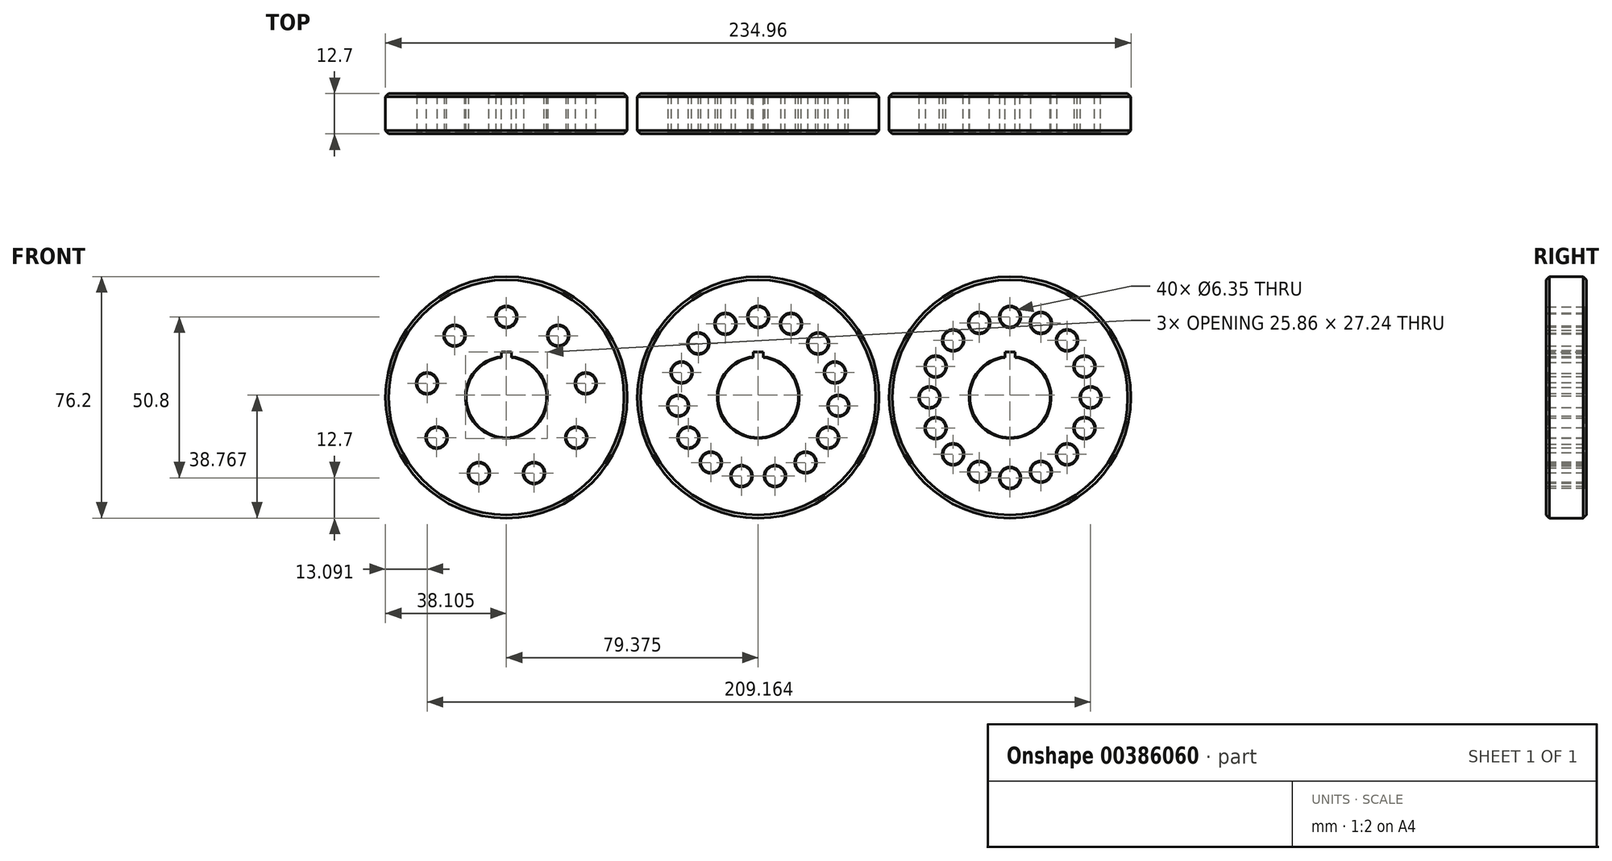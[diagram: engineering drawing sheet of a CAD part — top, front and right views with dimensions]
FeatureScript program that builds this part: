
annotation { "Feature Type Name" : "Feature", "Feature Type Description" : "" }
export const myFeature = defineFeature(function(context is Context, id is Id, definition is map)
    precondition{}
    {
        {
            var Q0;
            Q0=qCreatedBy(makeId("Front.planeOp"),FACE);
            var sketch = newSketch(context, id + "F0", { "sketchPlane" : qUnion([Q0])});
            skCircle(sketch, "E0", {"center": v(0, 0) * mm, "radius": 38.1 * mm});
            skCircle(sketch, "E1", {"center": v(-79.38, 0) * mm, "radius": 38.1 * mm});
            skCircle(sketch, "E2", {"center": v(79.38, 0) * mm, "radius": 38.1 * mm});
            skCircle(sketch, "E3", {"center": v(0, 25.4) * mm, "radius": 3.18 * mm});
            skCircle(sketch, "E4.1.0", {"center": v(-10.33, 23.2) * mm, "radius": 3.18 * mm});
            skCircle(sketch, "E4.2.0", {"center": v(-18.88, 17) * mm, "radius": 3.17 * mm});
            skCircle(sketch, "E4.3.0", {"center": v(-24.16, 7.85) * mm, "radius": 3.18 * mm});
            skCircle(sketch, "E4.4.0", {"center": v(-25.26, -2.66) * mm, "radius": 3.18 * mm});
            skCircle(sketch, "E4.5.0", {"center": v(-22, -12.7) * mm, "radius": 3.18 * mm});
            skCircle(sketch, "E4.6.0", {"center": v(-14.93, -20.55) * mm, "radius": 3.18 * mm});
            skCircle(sketch, "E4.7.0", {"center": v(-5.28, -24.84) * mm, "radius": 3.18 * mm});
            skCircle(sketch, "E4.8.0", {"center": v(5.28, -24.84) * mm, "radius": 3.18 * mm});
            skCircle(sketch, "E4.9.0", {"center": v(14.93, -20.55) * mm, "radius": 3.18 * mm});
            skCircle(sketch, "E4.10.0", {"center": v(22, -12.7) * mm, "radius": 3.18 * mm});
            skCircle(sketch, "E4.11.0", {"center": v(25.26, -2.66) * mm, "radius": 3.18 * mm});
            skCircle(sketch, "E4.12.0", {"center": v(24.16, 7.85) * mm, "radius": 3.18 * mm});
            skCircle(sketch, "E4.13.0", {"center": v(18.88, 17) * mm, "radius": 3.18 * mm});
            skCircle(sketch, "E4.14.0", {"center": v(10.33, 23.2) * mm, "radius": 3.18 * mm});
            skCircle(sketch, "E5", {"center": v(-79.38, 25.4) * mm, "radius": 3.18 * mm});
            skCircle(sketch, "E6.1.0", {"center": v(-95.7, 19.46) * mm, "radius": 3.18 * mm});
            skCircle(sketch, "E6.2.0", {"center": v(-104.39, 4.41) * mm, "radius": 3.18 * mm});
            skCircle(sketch, "E6.3.0", {"center": v(-101.37, -12.7) * mm, "radius": 3.18 * mm});
            skCircle(sketch, "E6.4.0", {"center": v(-88.06, -23.87) * mm, "radius": 3.18 * mm});
            skCircle(sketch, "E6.5.0", {"center": v(-70.69, -23.87) * mm, "radius": 3.18 * mm});
            skCircle(sketch, "E6.6.0", {"center": v(-57.38, -12.7) * mm, "radius": 3.18 * mm});
            skCircle(sketch, "E6.7.0", {"center": v(-54.36, 4.41) * mm, "radius": 3.18 * mm});
            skCircle(sketch, "E6.8.0", {"center": v(-63.05, 19.46) * mm, "radius": 3.18 * mm});
            skCircle(sketch, "E7", {"center": v(79.38, 25.4) * mm, "radius": 3.18 * mm});
            skCircle(sketch, "E8.1.0", {"center": v(69.65, 23.47) * mm, "radius": 3.18 * mm});
            skCircle(sketch, "E8.2.0", {"center": v(61.41, 17.96) * mm, "radius": 3.18 * mm});
            skCircle(sketch, "E8.3.0", {"center": v(55.9, 9.72) * mm, "radius": 3.18 * mm});
            skCircle(sketch, "E8.4.0", {"center": v(53.98, 0) * mm, "radius": 3.18 * mm});
            skCircle(sketch, "E8.5.0", {"center": v(55.9, -9.72) * mm, "radius": 3.18 * mm});
            skCircle(sketch, "E8.6.0", {"center": v(61.41, -17.96) * mm, "radius": 3.18 * mm});
            skCircle(sketch, "E8.7.0", {"center": v(69.65, -23.47) * mm, "radius": 3.18 * mm});
            skCircle(sketch, "E8.8.0", {"center": v(79.38, -25.4) * mm, "radius": 3.18 * mm});
            skCircle(sketch, "E8.9.0", {"center": v(89.1, -23.47) * mm, "radius": 3.18 * mm});
            skCircle(sketch, "E8.10.0", {"center": v(97.34, -17.96) * mm, "radius": 3.18 * mm});
            skCircle(sketch, "E8.11.0", {"center": v(102.84, -9.72) * mm, "radius": 3.18 * mm});
            skCircle(sketch, "E8.12.0", {"center": v(104.78, 0) * mm, "radius": 3.18 * mm});
            skCircle(sketch, "E8.13.0", {"center": v(102.84, 9.72) * mm, "radius": 3.18 * mm});
            skCircle(sketch, "E8.14.0", {"center": v(97.34, 17.96) * mm, "radius": 3.18 * mm});
            skCircle(sketch, "E8.15.0", {"center": v(89.1, 23.47) * mm, "radius": 3.18 * mm});
            skCircle(sketch, "E9", {"center": v(-79.38, 0) * mm, "radius": 12.7 * mm});
            skCircle(sketch, "E10", {"center": v(0, 0) * mm, "radius": 12.7 * mm});
            skCircle(sketch, "E11", {"center": v(79.38, 0) * mm, "radius": 12.7 * mm});
            skLineSegment(sketch, "E12.bottom", {"start": v(-77.79, 14.29) * mm, "end": v(-80.96, 14.29) * mm});
            skLineSegment(sketch, "E12.top", {"start": v(-77.79, 11.11) * mm, "end": v(-80.96, 11.11) * mm});
            skLineSegment(sketch, "E12.left", {"start": v(-77.79, 14.29) * mm, "end": v(-77.79, 11.11) * mm});
            skLineSegment(sketch, "E12.right", {"start": v(-80.96, 14.29) * mm, "end": v(-80.96, 11.11) * mm});
            skPoint(sketch, "E12.middle", {"position": v(-79.38, 12.7) * mm});
            skLineSegment(sketch, "E13.bottom", {"start": v(1.59, 14.29) * mm, "end": v(-1.59, 14.29) * mm});
            skLineSegment(sketch, "E13.top", {"start": v(1.59, 11.11) * mm, "end": v(-1.59, 11.11) * mm});
            skLineSegment(sketch, "E13.left", {"start": v(1.59, 14.29) * mm, "end": v(1.59, 11.11) * mm});
            skLineSegment(sketch, "E13.right", {"start": v(-1.59, 14.29) * mm, "end": v(-1.59, 11.11) * mm});
            skPoint(sketch, "E13.middle", {"position": v(0, 12.7) * mm});
            skLineSegment(sketch, "E14.bottom", {"start": v(80.96, 14.29) * mm, "end": v(77.79, 14.29) * mm});
            skLineSegment(sketch, "E14.top", {"start": v(80.96, 11.11) * mm, "end": v(77.79, 11.11) * mm});
            skLineSegment(sketch, "E14.left", {"start": v(80.96, 14.29) * mm, "end": v(80.96, 11.11) * mm});
            skLineSegment(sketch, "E14.right", {"start": v(77.79, 14.29) * mm, "end": v(77.79, 11.11) * mm});
            skPoint(sketch, "E14.middle", {"position": v(79.38, 12.7) * mm});
            skLineSegment(sketch, "E15", {"start": v(-63.05, 19.46) * mm, "end": v(-79.38, 0) * mm});
            skLineSegment(sketch, "E16", {"start": v(-54.36, 4.41) * mm, "end": v(-79.38, 0) * mm});
            skLineSegment(sketch, "E17", {"start": v(24.16, 7.85) * mm, "end": v(0, 0) * mm});
            skLineSegment(sketch, "E18", {"start": v(0, 0) * mm, "end": v(18.88, 17) * mm});
            skLineSegment(sketch, "E19", {"start": v(102.84, 9.72) * mm, "end": v(79.38, 0) * mm});
            skLineSegment(sketch, "E20", {"start": v(79.38, 0) * mm, "end": v(97.34, 17.96) * mm});
            skSolve(sketch);
        }
        {
            var Q0;
            Q0=makeQuery(id+"F0.imprint","IMPRINT",FACE,{"disambiguationData":[TD([[makeQuery(id+"F0.imprint","IMPRINT",EDGE,{"derivedFrom":sQuery(id+"F0.wireOp",EDGE,"E1")}),1.0]])]});
            var Q1;
            Q1=makeQuery(id+"F0.imprint","IMPRINT",FACE,{"disambiguationData":[TD([[makeQuery(id+"F0.imprint","IMPRINT",EDGE,{"derivedFrom":sQuery(id+"F0.wireOp",EDGE,"E0")}),1.0]])]});
            var Q2;
            Q2=makeQuery(id+"F0.imprint","IMPRINT",FACE,{"disambiguationData":[TD([[makeQuery(id+"F0.imprint","IMPRINT",EDGE,{"derivedFrom":sQuery(id+"F0.wireOp",EDGE,"E2")}),1.0]])]});
            extrude(context, id + "F1", {"entities" : qUnion([Q0, Q1, Q2]), "depth" : 12.7 * mm, "offsetDistance" : 25.4 * mm});
        }
        {
            var Q0;
            Q0=makeQuery(id+"F1.opExtrude","CAP_EDGE",EDGE,{"disambiguationData":[OSD([sQuery(id+"F0.wireOp",EDGE,"E1")])],"isStart":false});
            var Q1;
            Q1=makeQuery(id+"F1.opExtrude","CAP_EDGE",EDGE,{"disambiguationData":[OSD([sQuery(id+"F0.wireOp",EDGE,"E1")])],"isStart":true});
            var Q2;
            Q2=makeQuery(id+"F1.opExtrude","CAP_EDGE",EDGE,{"disambiguationData":[OSD([sQuery(id+"F0.wireOp",EDGE,"E0")])],"isStart":false});
            var Q3;
            Q3=makeQuery(id+"F1.opExtrude","CAP_EDGE",EDGE,{"disambiguationData":[OSD([sQuery(id+"F0.wireOp",EDGE,"E0")])],"isStart":true});
            var Q4;
            Q4=makeQuery(id+"F1.opExtrude","CAP_EDGE",EDGE,{"disambiguationData":[OSD([sQuery(id+"F0.wireOp",EDGE,"E2")])],"isStart":false});
            var Q5;
            Q5=makeQuery(id+"F1.opExtrude","CAP_EDGE",EDGE,{"disambiguationData":[OSD([sQuery(id+"F0.wireOp",EDGE,"E2")])],"isStart":true});
            chamfer(context, id + "F2", {"entities" : qUnion([Q0, Q1, Q2, Q3, Q4, Q5]), "width" : 1.02 * mm, "tangentPropagation" : true});
        }
        {
            var Q0;
            Q0=makeQuery(id+"F1.opExtrude","CAP_EDGE",EDGE,{"disambiguationData":[OSD([sQuery(id+"F0.wireOp",EDGE,"E6.2.0")])],"isStart":false});
            var Q1;
            Q1=makeQuery(id+"F1.opExtrude","CAP_EDGE",EDGE,{"disambiguationData":[OSD([sQuery(id+"F0.wireOp",EDGE,"E6.1.0")])],"isStart":false});
            var Q2;
            Q2=makeQuery(id+"F1.opExtrude","CAP_EDGE",EDGE,{"disambiguationData":[OSD([sQuery(id+"F0.wireOp",EDGE,"E5")])],"isStart":false});
            var Q3;
            Q3=makeQuery(id+"F1.opExtrude","CAP_EDGE",EDGE,{"disambiguationData":[OSD([sQuery(id+"F0.wireOp",EDGE,"E6.8.0")])],"isStart":false});
            var Q4;
            Q4=makeQuery(id+"F1.opExtrude","CAP_EDGE",EDGE,{"disambiguationData":[OSD([sQuery(id+"F0.wireOp",EDGE,"E6.7.0")])],"isStart":false});
            var Q5;
            Q5=makeQuery(id+"F1.opExtrude","CAP_EDGE",EDGE,{"disambiguationData":[OSD([sQuery(id+"F0.wireOp",EDGE,"E6.6.0")])],"isStart":false});
            var Q6;
            Q6=makeQuery(id+"F1.opExtrude","CAP_EDGE",EDGE,{"disambiguationData":[OSD([sQuery(id+"F0.wireOp",EDGE,"E6.5.0")])],"isStart":false});
            var Q7;
            Q7=makeQuery(id+"F1.opExtrude","CAP_EDGE",EDGE,{"disambiguationData":[OSD([sQuery(id+"F0.wireOp",EDGE,"E6.4.0")])],"isStart":false});
            var Q8;
            Q8=makeQuery(id+"F1.opExtrude","CAP_EDGE",EDGE,{"disambiguationData":[OSD([sQuery(id+"F0.wireOp",EDGE,"E6.3.0")])],"isStart":false});
            var Q9;
            Q9=makeQuery(id+"F1.opExtrude","CAP_EDGE",EDGE,{"disambiguationData":[OSD([sQuery(id+"F0.wireOp",EDGE,"E3")])],"isStart":false});
            var Q10;
            Q10=makeQuery(id+"F1.opExtrude","CAP_EDGE",EDGE,{"disambiguationData":[OSD([sQuery(id+"F0.wireOp",EDGE,"E4.14.0")])],"isStart":false});
            var Q11;
            Q11=makeQuery(id+"F1.opExtrude","CAP_EDGE",EDGE,{"disambiguationData":[OSD([sQuery(id+"F0.wireOp",EDGE,"E4.13.0")])],"isStart":false});
            var Q12;
            Q12=makeQuery(id+"F1.opExtrude","CAP_EDGE",EDGE,{"disambiguationData":[OSD([sQuery(id+"F0.wireOp",EDGE,"E4.12.0")])],"isStart":false});
            var Q13;
            Q13=makeQuery(id+"F1.opExtrude","CAP_EDGE",EDGE,{"disambiguationData":[OSD([sQuery(id+"F0.wireOp",EDGE,"E4.11.0")])],"isStart":false});
            var Q14;
            Q14=makeQuery(id+"F1.opExtrude","CAP_EDGE",EDGE,{"disambiguationData":[OSD([sQuery(id+"F0.wireOp",EDGE,"E4.10.0")])],"isStart":false});
            var Q15;
            Q15=makeQuery(id+"F1.opExtrude","CAP_EDGE",EDGE,{"disambiguationData":[OSD([sQuery(id+"F0.wireOp",EDGE,"E4.9.0")])],"isStart":false});
            var Q16;
            Q16=makeQuery(id+"F1.opExtrude","CAP_EDGE",EDGE,{"disambiguationData":[OSD([sQuery(id+"F0.wireOp",EDGE,"E4.8.0")])],"isStart":false});
            var Q17;
            Q17=makeQuery(id+"F1.opExtrude","CAP_EDGE",EDGE,{"disambiguationData":[OSD([sQuery(id+"F0.wireOp",EDGE,"E4.7.0")])],"isStart":false});
            var Q18;
            Q18=makeQuery(id+"F1.opExtrude","CAP_EDGE",EDGE,{"disambiguationData":[OSD([sQuery(id+"F0.wireOp",EDGE,"E4.6.0")])],"isStart":false});
            var Q19;
            Q19=makeQuery(id+"F1.opExtrude","CAP_EDGE",EDGE,{"disambiguationData":[OSD([sQuery(id+"F0.wireOp",EDGE,"E4.5.0")])],"isStart":false});
            var Q20;
            Q20=makeQuery(id+"F1.opExtrude","CAP_EDGE",EDGE,{"disambiguationData":[OSD([sQuery(id+"F0.wireOp",EDGE,"E4.4.0")])],"isStart":false});
            var Q21;
            Q21=makeQuery(id+"F1.opExtrude","CAP_EDGE",EDGE,{"disambiguationData":[OSD([sQuery(id+"F0.wireOp",EDGE,"E4.3.0")])],"isStart":false});
            var Q22;
            Q22=makeQuery(id+"F1.opExtrude","CAP_EDGE",EDGE,{"disambiguationData":[OSD([sQuery(id+"F0.wireOp",EDGE,"E4.2.0")])],"isStart":false});
            var Q23;
            Q23=makeQuery(id+"F1.opExtrude","CAP_EDGE",EDGE,{"disambiguationData":[OSD([sQuery(id+"F0.wireOp",EDGE,"E4.1.0")])],"isStart":false});
            var Q24;
            Q24=makeQuery(id+"F1.opExtrude","CAP_EDGE",EDGE,{"disambiguationData":[OSD([sQuery(id+"F0.wireOp",EDGE,"E7")])],"isStart":false});
            var Q25;
            Q25=makeQuery(id+"F1.opExtrude","CAP_EDGE",EDGE,{"disambiguationData":[OSD([sQuery(id+"F0.wireOp",EDGE,"E8.15.0")])],"isStart":false});
            var Q26;
            Q26=makeQuery(id+"F1.opExtrude","CAP_EDGE",EDGE,{"disambiguationData":[OSD([sQuery(id+"F0.wireOp",EDGE,"E8.14.0")])],"isStart":false});
            var Q27;
            Q27=makeQuery(id+"F1.opExtrude","CAP_EDGE",EDGE,{"disambiguationData":[OSD([sQuery(id+"F0.wireOp",EDGE,"E8.13.0")])],"isStart":false});
            var Q28;
            Q28=makeQuery(id+"F1.opExtrude","CAP_EDGE",EDGE,{"disambiguationData":[OSD([sQuery(id+"F0.wireOp",EDGE,"E8.12.0")])],"isStart":false});
            var Q29;
            Q29=makeQuery(id+"F1.opExtrude","CAP_EDGE",EDGE,{"disambiguationData":[OSD([sQuery(id+"F0.wireOp",EDGE,"E8.11.0")])],"isStart":false});
            var Q30;
            Q30=makeQuery(id+"F1.opExtrude","CAP_EDGE",EDGE,{"disambiguationData":[OSD([sQuery(id+"F0.wireOp",EDGE,"E8.10.0")])],"isStart":false});
            var Q31;
            Q31=makeQuery(id+"F1.opExtrude","CAP_EDGE",EDGE,{"disambiguationData":[OSD([sQuery(id+"F0.wireOp",EDGE,"E8.9.0")])],"isStart":false});
            var Q32;
            Q32=makeQuery(id+"F1.opExtrude","CAP_EDGE",EDGE,{"disambiguationData":[OSD([sQuery(id+"F0.wireOp",EDGE,"E8.8.0")])],"isStart":false});
            var Q33;
            Q33=makeQuery(id+"F1.opExtrude","CAP_EDGE",EDGE,{"disambiguationData":[OSD([sQuery(id+"F0.wireOp",EDGE,"E8.7.0")])],"isStart":false});
            var Q34;
            Q34=makeQuery(id+"F1.opExtrude","CAP_EDGE",EDGE,{"disambiguationData":[OSD([sQuery(id+"F0.wireOp",EDGE,"E8.6.0")])],"isStart":false});
            var Q35;
            Q35=makeQuery(id+"F1.opExtrude","CAP_EDGE",EDGE,{"disambiguationData":[OSD([sQuery(id+"F0.wireOp",EDGE,"E8.5.0")])],"isStart":false});
            var Q36;
            Q36=makeQuery(id+"F1.opExtrude","CAP_EDGE",EDGE,{"disambiguationData":[OSD([sQuery(id+"F0.wireOp",EDGE,"E8.4.0")])],"isStart":false});
            var Q37;
            Q37=makeQuery(id+"F1.opExtrude","CAP_EDGE",EDGE,{"disambiguationData":[OSD([sQuery(id+"F0.wireOp",EDGE,"E8.3.0")])],"isStart":false});
            var Q38;
            Q38=makeQuery(id+"F1.opExtrude","CAP_EDGE",EDGE,{"disambiguationData":[OSD([sQuery(id+"F0.wireOp",EDGE,"E8.2.0")])],"isStart":false});
            var Q39;
            Q39=makeQuery(id+"F1.opExtrude","CAP_EDGE",EDGE,{"disambiguationData":[OSD([sQuery(id+"F0.wireOp",EDGE,"E8.1.0")])],"isStart":false});
            var Q40;
            Q40=makeQuery(id+"F1.opExtrude","CAP_EDGE",EDGE,{"disambiguationData":[OSD([sQuery(id+"F0.wireOp",EDGE,"E6.4.0")])],"isStart":true});
            var Q41;
            Q41=makeQuery(id+"F1.opExtrude","CAP_EDGE",EDGE,{"disambiguationData":[OSD([sQuery(id+"F0.wireOp",EDGE,"E6.5.0")])],"isStart":true});
            var Q42;
            Q42=makeQuery(id+"F1.opExtrude","CAP_EDGE",EDGE,{"disambiguationData":[OSD([sQuery(id+"F0.wireOp",EDGE,"E6.6.0")])],"isStart":true});
            var Q43;
            Q43=makeQuery(id+"F1.opExtrude","CAP_EDGE",EDGE,{"disambiguationData":[OSD([sQuery(id+"F0.wireOp",EDGE,"E6.7.0")])],"isStart":true});
            var Q44;
            Q44=makeQuery(id+"F1.opExtrude","CAP_EDGE",EDGE,{"disambiguationData":[OSD([sQuery(id+"F0.wireOp",EDGE,"E6.8.0")])],"isStart":true});
            var Q45;
            Q45=makeQuery(id+"F1.opExtrude","CAP_EDGE",EDGE,{"disambiguationData":[OSD([sQuery(id+"F0.wireOp",EDGE,"E5")])],"isStart":true});
            var Q46;
            Q46=makeQuery(id+"F1.opExtrude","CAP_EDGE",EDGE,{"disambiguationData":[OSD([sQuery(id+"F0.wireOp",EDGE,"E6.1.0")])],"isStart":true});
            var Q47;
            Q47=makeQuery(id+"F1.opExtrude","CAP_EDGE",EDGE,{"disambiguationData":[OSD([sQuery(id+"F0.wireOp",EDGE,"E6.2.0")])],"isStart":true});
            var Q48;
            Q48=makeQuery(id+"F1.opExtrude","CAP_EDGE",EDGE,{"disambiguationData":[OSD([sQuery(id+"F0.wireOp",EDGE,"E6.3.0")])],"isStart":true});
            var Q49;
            Q49=makeQuery(id+"F1.opExtrude","CAP_EDGE",EDGE,{"disambiguationData":[OSD([sQuery(id+"F0.wireOp",EDGE,"E4.7.0")])],"isStart":true});
            var Q50;
            Q50=makeQuery(id+"F1.opExtrude","CAP_EDGE",EDGE,{"disambiguationData":[OSD([sQuery(id+"F0.wireOp",EDGE,"E4.8.0")])],"isStart":true});
            var Q51;
            Q51=makeQuery(id+"F1.opExtrude","CAP_EDGE",EDGE,{"disambiguationData":[OSD([sQuery(id+"F0.wireOp",EDGE,"E4.9.0")])],"isStart":true});
            var Q52;
            Q52=makeQuery(id+"F1.opExtrude","CAP_EDGE",EDGE,{"disambiguationData":[OSD([sQuery(id+"F0.wireOp",EDGE,"E4.10.0")])],"isStart":true});
            var Q53;
            Q53=makeQuery(id+"F1.opExtrude","CAP_EDGE",EDGE,{"disambiguationData":[OSD([sQuery(id+"F0.wireOp",EDGE,"E4.11.0")])],"isStart":true});
            var Q54;
            Q54=makeQuery(id+"F1.opExtrude","CAP_EDGE",EDGE,{"disambiguationData":[OSD([sQuery(id+"F0.wireOp",EDGE,"E4.12.0")])],"isStart":true});
            var Q55;
            Q55=makeQuery(id+"F1.opExtrude","CAP_EDGE",EDGE,{"disambiguationData":[OSD([sQuery(id+"F0.wireOp",EDGE,"E4.13.0")])],"isStart":true});
            var Q56;
            Q56=makeQuery(id+"F1.opExtrude","CAP_EDGE",EDGE,{"disambiguationData":[OSD([sQuery(id+"F0.wireOp",EDGE,"E4.14.0")])],"isStart":true});
            var Q57;
            Q57=makeQuery(id+"F1.opExtrude","CAP_EDGE",EDGE,{"disambiguationData":[OSD([sQuery(id+"F0.wireOp",EDGE,"E3")])],"isStart":true});
            var Q58;
            Q58=makeQuery(id+"F1.opExtrude","CAP_EDGE",EDGE,{"disambiguationData":[OSD([sQuery(id+"F0.wireOp",EDGE,"E4.1.0")])],"isStart":true});
            var Q59;
            Q59=makeQuery(id+"F1.opExtrude","CAP_EDGE",EDGE,{"disambiguationData":[OSD([sQuery(id+"F0.wireOp",EDGE,"E4.2.0")])],"isStart":true});
            var Q60;
            Q60=makeQuery(id+"F1.opExtrude","CAP_EDGE",EDGE,{"disambiguationData":[OSD([sQuery(id+"F0.wireOp",EDGE,"E4.3.0")])],"isStart":true});
            var Q61;
            Q61=makeQuery(id+"F1.opExtrude","CAP_EDGE",EDGE,{"disambiguationData":[OSD([sQuery(id+"F0.wireOp",EDGE,"E4.4.0")])],"isStart":true});
            var Q62;
            Q62=makeQuery(id+"F1.opExtrude","CAP_EDGE",EDGE,{"disambiguationData":[OSD([sQuery(id+"F0.wireOp",EDGE,"E4.5.0")])],"isStart":true});
            var Q63;
            Q63=makeQuery(id+"F1.opExtrude","CAP_EDGE",EDGE,{"disambiguationData":[OSD([sQuery(id+"F0.wireOp",EDGE,"E4.6.0")])],"isStart":true});
            var Q64;
            Q64=makeQuery(id+"F1.opExtrude","CAP_EDGE",EDGE,{"disambiguationData":[OSD([sQuery(id+"F0.wireOp",EDGE,"E8.7.0")])],"isStart":true});
            var Q65;
            Q65=makeQuery(id+"F1.opExtrude","CAP_EDGE",EDGE,{"disambiguationData":[OSD([sQuery(id+"F0.wireOp",EDGE,"E8.8.0")])],"isStart":true});
            var Q66;
            Q66=makeQuery(id+"F1.opExtrude","CAP_EDGE",EDGE,{"disambiguationData":[OSD([sQuery(id+"F0.wireOp",EDGE,"E8.9.0")])],"isStart":true});
            var Q67;
            Q67=makeQuery(id+"F1.opExtrude","CAP_EDGE",EDGE,{"disambiguationData":[OSD([sQuery(id+"F0.wireOp",EDGE,"E8.10.0")])],"isStart":true});
            var Q68;
            Q68=makeQuery(id+"F1.opExtrude","CAP_EDGE",EDGE,{"disambiguationData":[OSD([sQuery(id+"F0.wireOp",EDGE,"E8.11.0")])],"isStart":true});
            var Q69;
            Q69=makeQuery(id+"F1.opExtrude","CAP_EDGE",EDGE,{"disambiguationData":[OSD([sQuery(id+"F0.wireOp",EDGE,"E8.12.0")])],"isStart":true});
            var Q70;
            Q70=makeQuery(id+"F1.opExtrude","CAP_EDGE",EDGE,{"disambiguationData":[OSD([sQuery(id+"F0.wireOp",EDGE,"E8.13.0")])],"isStart":true});
            var Q71;
            Q71=makeQuery(id+"F1.opExtrude","CAP_EDGE",EDGE,{"disambiguationData":[OSD([sQuery(id+"F0.wireOp",EDGE,"E8.14.0")])],"isStart":true});
            var Q72;
            Q72=makeQuery(id+"F1.opExtrude","CAP_EDGE",EDGE,{"disambiguationData":[OSD([sQuery(id+"F0.wireOp",EDGE,"E8.15.0")])],"isStart":true});
            var Q73;
            Q73=makeQuery(id+"F1.opExtrude","CAP_EDGE",EDGE,{"disambiguationData":[OSD([sQuery(id+"F0.wireOp",EDGE,"E7")])],"isStart":true});
            var Q74;
            Q74=makeQuery(id+"F1.opExtrude","CAP_EDGE",EDGE,{"disambiguationData":[OSD([sQuery(id+"F0.wireOp",EDGE,"E8.1.0")])],"isStart":true});
            var Q75;
            Q75=makeQuery(id+"F1.opExtrude","CAP_EDGE",EDGE,{"disambiguationData":[OSD([sQuery(id+"F0.wireOp",EDGE,"E8.2.0")])],"isStart":true});
            var Q76;
            Q76=makeQuery(id+"F1.opExtrude","CAP_EDGE",EDGE,{"disambiguationData":[OSD([sQuery(id+"F0.wireOp",EDGE,"E8.3.0")])],"isStart":true});
            var Q77;
            Q77=makeQuery(id+"F1.opExtrude","CAP_EDGE",EDGE,{"disambiguationData":[OSD([sQuery(id+"F0.wireOp",EDGE,"E8.4.0")])],"isStart":true});
            var Q78;
            Q78=makeQuery(id+"F1.opExtrude","CAP_EDGE",EDGE,{"disambiguationData":[OSD([sQuery(id+"F0.wireOp",EDGE,"E8.5.0")])],"isStart":true});
            var Q79;
            Q79=makeQuery(id+"F1.opExtrude","CAP_EDGE",EDGE,{"disambiguationData":[OSD([sQuery(id+"F0.wireOp",EDGE,"E8.6.0")])],"isStart":true});
            var Q80;
            Q80=makeQuery(id+"F1.opExtrude","CAP_EDGE",EDGE,{"disambiguationData":[OSD([sQuery(id+"F0.wireOp",EDGE,"E9")])],"isStart":false});
            var Q81;
            Q81=makeQuery(id+"F1.opExtrude","CAP_EDGE",EDGE,{"disambiguationData":[OSD([sQuery(id+"F0.wireOp",EDGE,"E10")])],"isStart":false});
            var Q82;
            Q82=makeQuery(id+"F1.opExtrude","CAP_EDGE",EDGE,{"disambiguationData":[OSD([sQuery(id+"F0.wireOp",EDGE,"E11")])],"isStart":false});
            var Q83;
            Q83=makeQuery(id+"F1.opExtrude","CAP_EDGE",EDGE,{"disambiguationData":[OSD([sQuery(id+"F0.wireOp",EDGE,"E9")])],"isStart":true});
            var Q84;
            Q84=makeQuery(id+"F1.opExtrude","CAP_EDGE",EDGE,{"disambiguationData":[OSD([sQuery(id+"F0.wireOp",EDGE,"E10")])],"isStart":true});
            var Q85;
            Q85=makeQuery(id+"F1.opExtrude","CAP_EDGE",EDGE,{"disambiguationData":[OSD([sQuery(id+"F0.wireOp",EDGE,"E11")])],"isStart":true});
            chamfer(context, id + "F3", {"entities" : qUnion([Q0, Q1, Q2, Q3, Q4, Q5, Q6, Q7, Q8, Q9, Q10, Q11, Q12, Q13, Q14, Q15, Q16, Q17, Q18, Q19, Q20, Q21, Q22, Q23, Q24, Q25, Q26, Q27, Q28, Q29, Q30, Q31, Q32, Q33, Q34, Q35, Q36, Q37, Q38, Q39, Q40, Q41, Q42, Q43, Q44, Q45, Q46, Q47, Q48, Q49, Q50, Q51, Q52, Q53, Q54, Q55, Q56, Q57, Q58, Q59, Q60, Q61, Q62, Q63, Q64, Q65, Q66, Q67, Q68, Q69, Q70, Q71, Q72, Q73, Q74, Q75, Q76, Q77, Q78, Q79, Q80, Q81, Q82, Q83, Q84, Q85]), "width" : 0.25 * mm, "tangentPropagation" : true});
        }
    });
